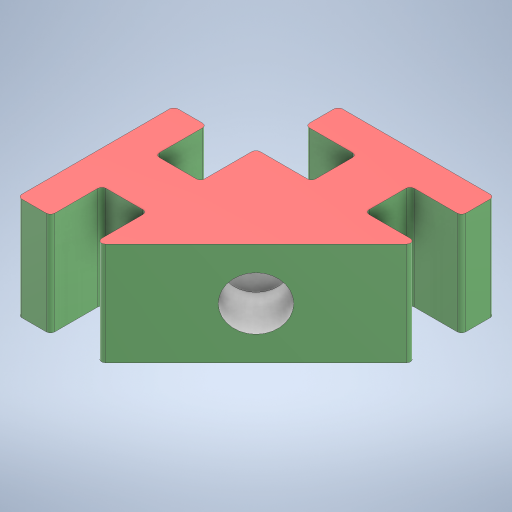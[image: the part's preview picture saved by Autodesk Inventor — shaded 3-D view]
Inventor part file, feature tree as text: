
AUTODESK INVENTOR PART (.ipt)
format: ipt  version: 2023 (Build 270158000, 158)  size: 268,288 bytes
history: native  units: in
note: dims shown in document units (in); Inventor stores cm internally (conversion verified against a paired STEP export)
features: other x4, extrude x1, sketch x1
ambient origin geometry x8: Origin, YZ Plane, XZ Plane, XY Plane, X Axis, Y Axis, Z Axis, Center Point
bodies: Body1 (feature_tree)
feature tree (6):
  other  "FlexPart.ipt"
  extrude  "Extrusion1"  Depth=0.1024in
  other  "PLA2::FlexPart.ipt"
  other  "TaggingFeature1"
  sketch  "Sketch1"  dims[d0=0.3937in d1=0.1024in d2=0.0984in d3=0.0in]
  other  "PLA2"
